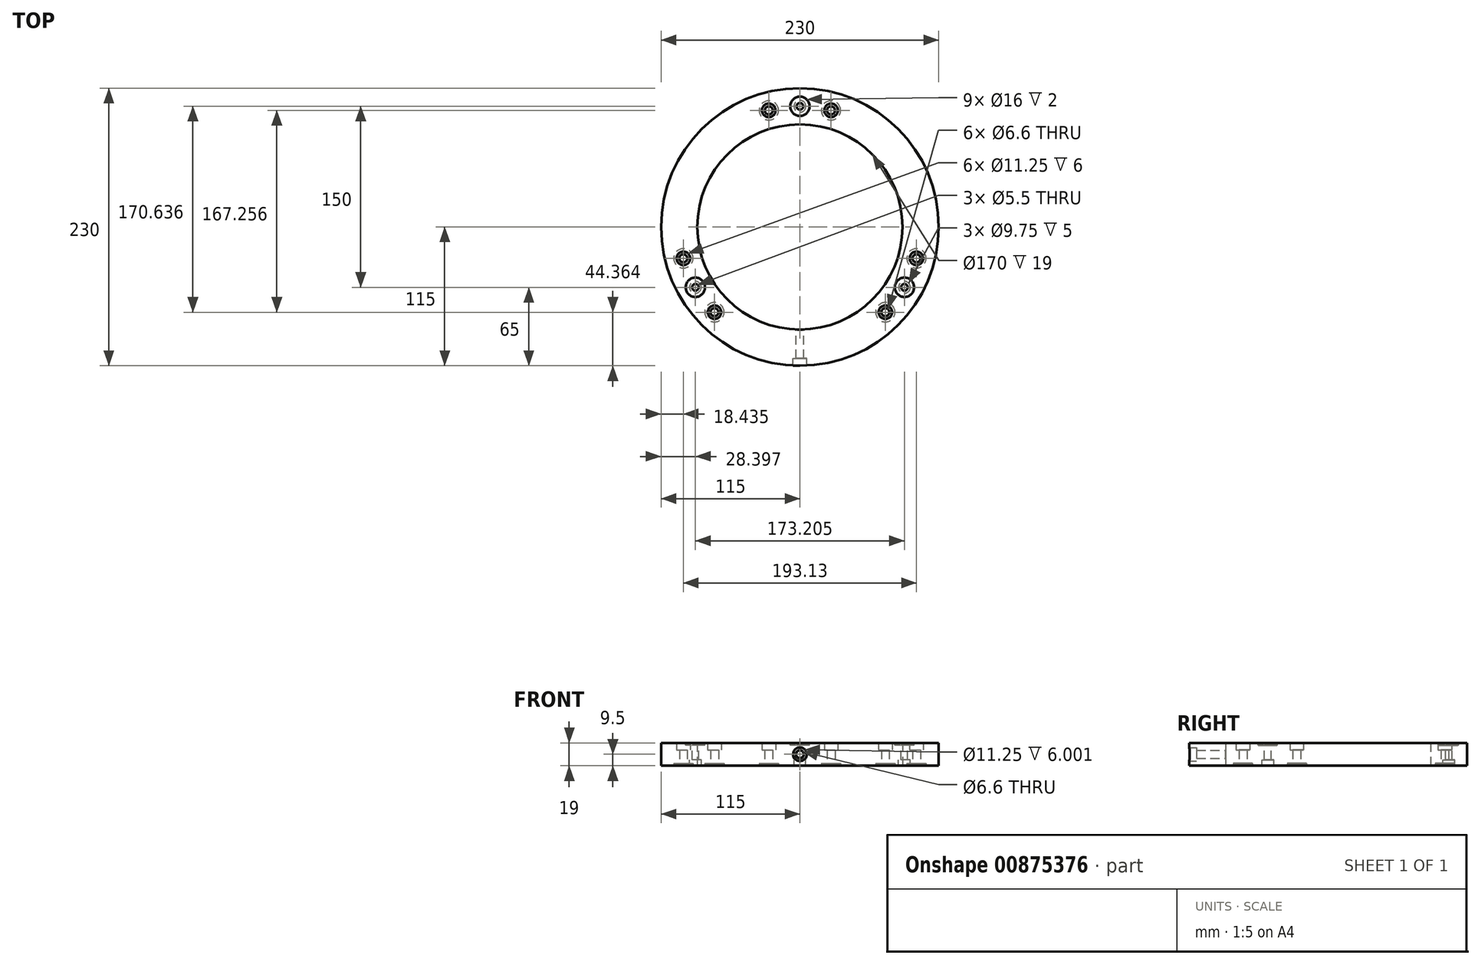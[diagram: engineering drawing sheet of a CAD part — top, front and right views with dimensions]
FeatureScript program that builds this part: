
annotation { "Feature Type Name" : "Feature", "Feature Type Description" : "" }
export const myFeature = defineFeature(function(context is Context, id is Id, definition is map)
    precondition{}
    {
        {
            var Q0;
            Q0=qCreatedBy(makeId("Top.planeOp"),FACE);
            var sketch = newSketch(context, id + "F0", { "sketchPlane" : qUnion([Q0])});
            skCircle(sketch, "E0", {"center": v(0, 0) * mm, "radius": 85 * mm});
            skCircle(sketch, "E1.0", {"center": v(0, 0) * mm, "radius": 115 * mm});
            skSolve(sketch);
        }
        {
            var Q0;
            Q0=makeQuery(id+"F0.imprint","IMPRINT",FACE,{"disambiguationData":[TD([[makeQuery(id+"F0.imprint","IMPRINT",EDGE,{"derivedFrom":sQuery(id+"F0.wireOp",EDGE,"E0")}),-1.0]])]});
            extrude(context, id + "F1", {"entities" : qUnion([Q0]), "depth" : 19 * mm, "offsetDistance" : 25 * mm});
        }
        {
            var Q0;
            Q0=makeQuery(id+"F1.opExtrude","CAP_FACE",FACE,{"disambiguationData":[OSD([sQuery(id+"F0.wireOp",EDGE,"E0"),sQuery(id+"F0.wireOp",EDGE,"E1.0")])],"isStart":true});
            var sketch = newSketch(context, id + "F2", { "sketchPlane" : qUnion([Q0])});
            skLineSegment(sketch, "E2", {"start": v(0, -85) * mm, "end": v(0, -115) * mm, "construction": true});
            skPoint(sketch, "E3", {"position": v(0, -100) * mm});
            skPoint(sketch, "E4.1.0", {"position": v(86.6, 50) * mm});
            skPoint(sketch, "E4.2.0", {"position": v(-86.6, 50) * mm});
            skPoint(sketch, "E4.center", {"position": v(0, 0) * mm});
            skSolve(sketch);
        }
        {
            var Q0;
            Q0=sQuery(id+"F2.wireOp",VERTEX,"E3");
            var Q1;
            Q1=sQuery(id+"F2.wireOp",VERTEX,"E4.1.0");
            var Q2;
            Q2=sQuery(id+"F2.wireOp",VERTEX,"E4.2.0");
            var Q3;
            Q3=makeQuery(id+"F1.opExtrude","SWEPT_BODY",BODY,{"disambiguationData":[OSD([sQuery(id+"F0.wireOp",EDGE,"E0"),sQuery(id+"F0.wireOp",EDGE,"E1.0")])]});
            hole(context, id + "F3", {"style" : HoleStyle.C_BORE, "endStyle" : HoleEndStyle.THROUGH, "standardTappedOrClearance" : lookupTablePath({ "fit" : "Normal", "standard" : "ISO", "size" : "M5", "type" : "Clearance" }), "standardBlindInLast" : lookupTablePath({ "fit" : "Normal", "standard" : "ISO", "size" : "M5", "type" : "Clearance" }), "holeDiameter" : 5.5 * mm, "cBoreDiameter" : 9.75 * mm, "cBoreDepth" : 5 * mm, "majorDiameter" : 5 * mm, "isTappedThrough" : true, "tappedDepth" : 12 * mm, "tapClearance" : 3, "locations" : qUnion([Q0, Q1, Q2]), "scope" : qUnion([Q3]), "startStyle" : HoleStartStyle.SKETCH});
        }
        {
            var Q0;
            Q0=makeQuery(id+"F1.opExtrude","CAP_FACE",FACE,{"disambiguationData":[OSD([sQuery(id+"F0.wireOp",EDGE,"E0"),sQuery(id+"F0.wireOp",EDGE,"E1.0")])],"isStart":false});
            var sketch = newSketch(context, id + "F4", { "sketchPlane" : qUnion([Q0])});
            skPoint(sketch, "E5.center", {"position": v(0, 0) * mm});
            skLineSegment(sketch, "E6", {"start": v(0, 115) * mm, "end": v(0, 85) * mm, "construction": true});
            skCircle(sketch, "E7", {"center": v(0, 100) * mm, "radius": 8 * mm});
            skCircle(sketch, "E8.1.0", {"center": v(-86.6, -50) * mm, "radius": 8 * mm});
            skCircle(sketch, "E8.2.0", {"center": v(86.6, -50) * mm, "radius": 8 * mm});
            skSolve(sketch);
        }
        {
            var Q0;
            Q0 = qSketchRegion(id + "F4", true);
            extrude(context, id + "F5", {"entities" : qUnion([Q0]), "operationType" : NewBodyOperationType.REMOVE, "oppositeDirection" : true, "depth" : 2 * mm, "offsetDistance" : 25 * mm});
        }
        {
            var Q0;
            Q0=qCreatedBy(makeId("Front.planeOp"),FACE);
            cPlane(context, id + "F6", {"entities" : qUnion([Q0]), "cplaneType" : CPlaneType.OFFSET, "offset" : 115 * mm, "width" : 150 * mm, "height" : 150 * mm});
        }
        {
            var Q0;
            Q0=qCreatedBy(id+"F6.planeOp",FACE);
            var sketch = newSketch(context, id + "F7", { "sketchPlane" : qUnion([Q0])});
            skLineSegment(sketch, "E9", {"start": v(0, 0) * mm, "end": v(0, 19) * mm, "construction": true});
            skPoint(sketch, "E10", {"position": v(0, 9.5) * mm});
            skSolve(sketch);
        }
        {
            var Q0;
            Q0=sQuery(id+"F7.wireOp",VERTEX,"E10");
            var Q1;
            Q1=makeQuery(id+"F1.opExtrude","SWEPT_BODY",BODY,{"disambiguationData":[OSD([sQuery(id+"F0.wireOp",EDGE,"E0"),sQuery(id+"F0.wireOp",EDGE,"E1.0")])]});
            hole(context, id + "F8", {"style" : HoleStyle.C_BORE, "endStyle" : HoleEndStyle.BLIND, "standardTappedOrClearance" : lookupTablePath({ "fit" : "Normal", "standard" : "ISO", "size" : "M6", "type" : "Clearance" }), "standardBlindInLast" : lookupTablePath({ "fit" : "Normal", "standard" : "ISO", "size" : "M6", "type" : "Clearance" }), "holeDiameter" : 6.6 * mm, "cBoreDiameter" : 11.25 * mm, "cBoreDepth" : 6 * mm, "majorDiameter" : 6 * mm, "holeDepth" : 30 * mm, "isTappedThrough" : true, "tappedDepth" : 12 * mm, "tapClearance" : 3, "locations" : qUnion([Q0]), "scope" : qUnion([Q1]), "startStyle" : HoleStartStyle.SKETCH});
        }
        {
            var Q0;
            Q0=qCreatedBy(makeId("Front.planeOp"),FACE);
            var sketch = newSketch(context, id + "F9", { "sketchPlane" : qUnion([Q0])});
            skLineSegment(sketch, "E11", {"start": v(0, 0) * mm, "end": v(0, 42.86) * mm, "construction": true});
            skSolve(sketch);
        }
        {
            var Q0;
            Q0=makeQuery(id+"F1.opExtrude","CAP_FACE",FACE,{"disambiguationData":[OSD([sQuery(id+"F0.wireOp",EDGE,"E0"),sQuery(id+"F0.wireOp",EDGE,"E1.0")])],"isStart":true});
            var sketch = newSketch(context, id + "F10", { "sketchPlane" : qUnion([Q0])});
            skLineSegment(sketch, "E12", {"start": v(0, 0) * mm, "end": v(0, 118.08) * mm, "construction": true});
            skCircle(sketch, "E13", {"center": v(0, 0) * mm, "radius": 100 * mm, "construction": true});
            skCircle(sketch, "E14", {"center": v(25.78, -96.62) * mm, "radius": 8 * mm});
            skCircle(sketch, "E15.MirrorC", {"center": v(-25.78, -96.62) * mm, "radius": 8 * mm});
            skCircle(sketch, "E16.1.0", {"center": v(70.79, 70.64) * mm, "radius": 8 * mm});
            skCircle(sketch, "E16.1.1", {"center": v(96.57, 25.98) * mm, "radius": 8 * mm});
            skCircle(sketch, "E16.2.0", {"center": v(-96.57, 25.98) * mm, "radius": 8 * mm});
            skCircle(sketch, "E16.2.1", {"center": v(-70.79, 70.64) * mm, "radius": 8 * mm});
            skSolve(sketch);
        }
        {
            var Q0;
            Q0 = qSketchRegion(id + "F10", true);
            extrude(context, id + "F11", {"entities" : qUnion([Q0]), "operationType" : NewBodyOperationType.REMOVE, "oppositeDirection" : true, "depth" : 2 * mm, "offsetDistance" : 25 * mm});
        }
        {
            var Q0;
            Q0=makeQuery(id+"F1.opExtrude","CAP_FACE",FACE,{"disambiguationData":[OSD([sQuery(id+"F0.wireOp",EDGE,"E0"),sQuery(id+"F0.wireOp",EDGE,"E1.0")])],"isStart":false});
            var sketch = newSketch(context, id + "F12", { "sketchPlane" : qUnion([Q0])});
            skCircle(sketch, "E17", {"center": v(0, 0) * mm, "radius": 100 * mm, "construction": true});
            skCircle(sketch, "E18", {"center": v(25.78, 96.62) * mm, "radius": 8 * mm, "construction": true});
            skCircle(sketch, "E19.MirrorC", {"center": v(-25.78, 96.62) * mm, "radius": 8 * mm, "construction": true});
            skCircle(sketch, "E20.1.0", {"center": v(-70.79, -70.64) * mm, "radius": 8 * mm, "construction": true});
            skCircle(sketch, "E20.1.1", {"center": v(-96.57, -25.98) * mm, "radius": 8 * mm, "construction": true});
            skCircle(sketch, "E20.2.0", {"center": v(96.57, -25.98) * mm, "radius": 8 * mm, "construction": true});
            skCircle(sketch, "E20.2.1", {"center": v(70.79, -70.64) * mm, "radius": 8 * mm, "construction": true});
            skSolve(sketch);
        }
        {
            var Q0;
            Q0=sQuery(id+"F12.wireOp",VERTEX,"E20.1.1.center");
            var Q1;
            Q1=sQuery(id+"F12.wireOp",VERTEX,"E20.1.0.center");
            var Q2;
            Q2=sQuery(id+"F12.wireOp",VERTEX,"E20.2.1.center");
            var Q3;
            Q3=sQuery(id+"F12.wireOp",VERTEX,"E20.2.0.center");
            var Q4;
            Q4=sQuery(id+"F12.wireOp",VERTEX,"E18.center");
            var Q5;
            Q5=sQuery(id+"F12.wireOp",VERTEX,"E19.MirrorC.center");
            var Q6;
            Q6=makeQuery(id+"F1.opExtrude","SWEPT_BODY",BODY,{"disambiguationData":[OSD([sQuery(id+"F0.wireOp",EDGE,"E0"),sQuery(id+"F0.wireOp",EDGE,"E1.0")])]});
            hole(context, id + "F13", {"style" : HoleStyle.C_BORE, "endStyle" : HoleEndStyle.THROUGH, "standardTappedOrClearance" : lookupTablePath({ "fit" : "Normal", "standard" : "ISO", "size" : "M6", "type" : "Clearance" }), "standardBlindInLast" : lookupTablePath({ "fit" : "Normal", "standard" : "ISO", "engagement" : "75%", "pitch" : "1 mm", "size" : "M6", "type" : "Clearance & tapped" }), "holeDiameter" : 6.6 * mm, "cBoreDiameter" : 11.25 * mm, "cBoreDepth" : 6 * mm, "majorDiameter" : 5 * mm, "isTappedThrough" : true, "tappedDepth" : 12 * mm, "tapClearance" : 3, "locations" : qUnion([Q0, Q1, Q2, Q3, Q4, Q5]), "scope" : qUnion([Q6]), "startStyle" : HoleStartStyle.SKETCH});
        }
    });
